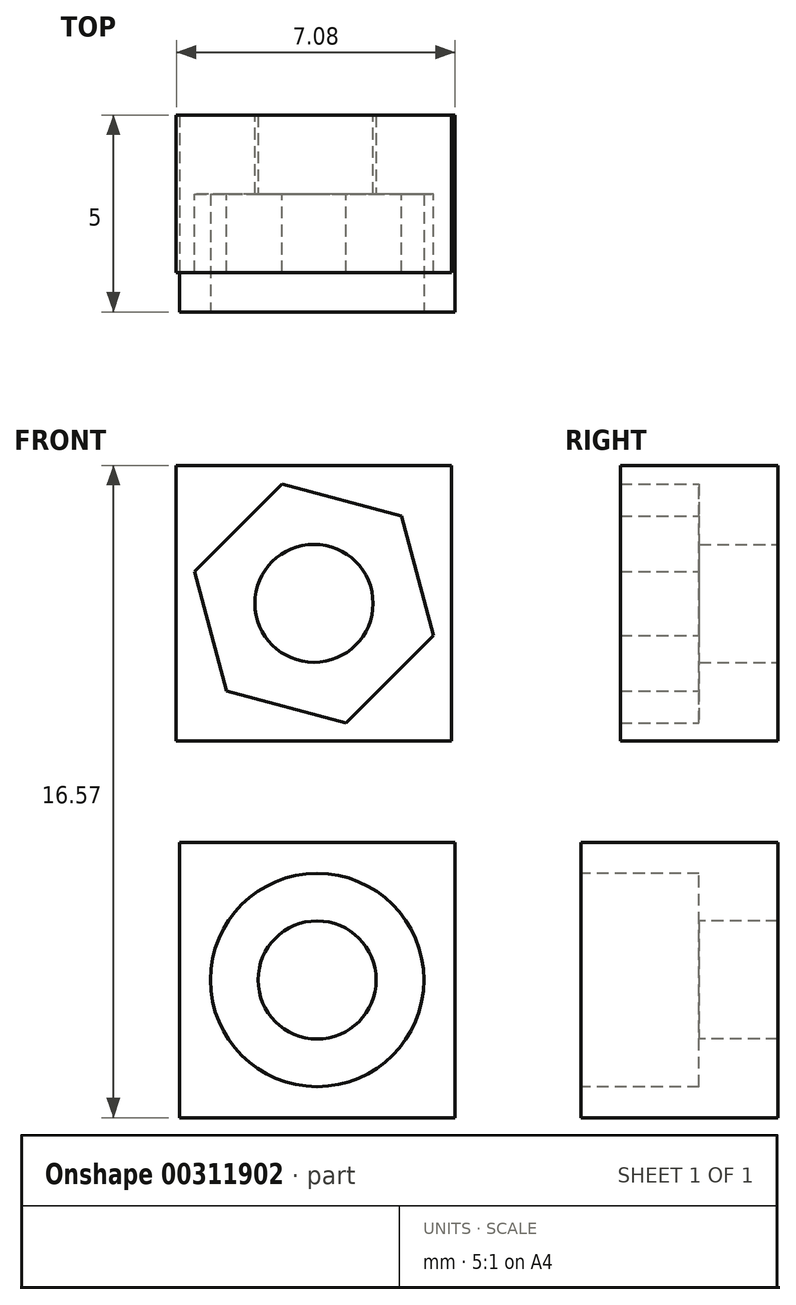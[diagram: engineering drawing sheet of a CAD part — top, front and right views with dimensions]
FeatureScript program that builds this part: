
annotation { "Feature Type Name" : "Feature", "Feature Type Description" : "" }
export const myFeature = defineFeature(function(context is Context, id is Id, definition is map)
    precondition{}
    {
        {
            var Q0;
            Q0=qCreatedBy(makeId("Front.planeOp"),FACE);
            var sketch = newSketch(context, id + "F0", { "sketchPlane" : qUnion([Q0])});
            skLineSegment(sketch, "E0.bottom", {"start": v(-25.27, 11.32) * mm, "end": v(-18.27, 11.32) * mm});
            skLineSegment(sketch, "E0.top", {"start": v(-25.27, 4.32) * mm, "end": v(-18.27, 4.32) * mm});
            skLineSegment(sketch, "E0.left", {"start": v(-25.27, 11.32) * mm, "end": v(-25.27, 4.32) * mm});
            skLineSegment(sketch, "E0.right", {"start": v(-18.27, 11.32) * mm, "end": v(-18.27, 4.32) * mm});
            skLineSegment(sketch, "E1", {"start": v(-25.27, 11.32) * mm, "end": v(-18.27, 4.32) * mm});
            skLineSegment(sketch, "E2", {"start": v(-18.27, 11.32) * mm, "end": v(-25.27, 4.32) * mm});
            skCircle(sketch, "E3", {"center": v(-21.77, 7.82) * mm, "radius": 2.7 * mm});
            skSolve(sketch);
        }
        {
            var Q0;
            {var subQ0=sQuery(id+"F0.wireOp",EDGE,"E0.bottom");Q0=makeQuery(id+"F0.imprint","IMPRINT",FACE,{"disambiguationData":[TD([[makeQuery(id+"F0.imprint","IMPRINT",EDGE,{"derivedFrom":subQ0}),-1.0]])]});}
            var Q1;
            {var subQ0=sQuery(id+"F0.wireOp",EDGE,"E0.left");Q1=makeQuery(id+"F0.imprint","IMPRINT",FACE,{"disambiguationData":[TD([[makeQuery(id+"F0.imprint","IMPRINT",EDGE,{"derivedFrom":subQ0}),1.0]])]});}
            var Q2;
            {var subQ0=sQuery(id+"F0.wireOp",EDGE,"E0.top");Q2=makeQuery(id+"F0.imprint","IMPRINT",FACE,{"disambiguationData":[TD([[makeQuery(id+"F0.imprint","IMPRINT",EDGE,{"derivedFrom":subQ0}),1.0]])]});}
            var Q3;
            {var subQ0=sQuery(id+"F0.wireOp",EDGE,"E0.right");Q3=makeQuery(id+"F0.imprint","IMPRINT",FACE,{"disambiguationData":[TD([[makeQuery(id+"F0.imprint","IMPRINT",EDGE,{"derivedFrom":subQ0}),-1.0]])]});}
            extrude(context, id + "F1", {"entities" : qUnion([Q0, Q1, Q2, Q3]), "oppositeDirection" : true, "depth" : 3 * mm});
        }
        {
            var Q0;
            Q0=makeQuery(id+"F1.opExtrude","CAP_FACE",FACE,{"disambiguationData":[OSD([sQuery(id+"F0.wireOp",EDGE,"E0.bottom"),sQuery(id+"F0.wireOp",EDGE,"E0.top"),sQuery(id+"F0.wireOp",EDGE,"E0.left"),sQuery(id+"F0.wireOp",EDGE,"E0.right"),sQuery(id+"F0.wireOp",EDGE,"E3")])],"isStart":false});
            var sketch = newSketch(context, id + "F2", { "sketchPlane" : qUnion([Q0])});
            skLineSegment(sketch, "E4", {"start": v(18.27, 11.32) * mm, "end": v(25.27, 4.32) * mm});
            skLineSegment(sketch, "E5", {"start": v(25.27, 4.32) * mm, "end": v(25.27, 11.32) * mm});
            skLineSegment(sketch, "E6", {"start": v(25.27, 11.32) * mm, "end": v(18.27, 4.32) * mm});
            skCircle(sketch, "E7", {"center": v(21.77, 7.82) * mm, "radius": 1.5 * mm});
            skSolve(sketch);
        }
        {
            var Q0;
            {var subQ1=makeQuery(id+"F1.opExtrude","CAP_EDGE",EDGE,{"disambiguationData":[OSD([sQuery(id+"F0.wireOp",EDGE,"E0.right")])],"isStart":false});Q0=makeQuery(id+"F2.imprint","IMPRINT",FACE,{"disambiguationData":[TD([[makeQuery(id+"F2.imprint","IMPRINT",EDGE,{"derivedFrom":subQ1}),1.0]])]});}
            var Q1;
            {var subQ0=sQuery(id+"F2.wireOp",EDGE,"E7");var subQ1=sQuery(id+"F2.wireOp",EDGE,"E4");var subQ2=makeQuery(id+"F2.imprint","INTERSECT",VERTEX,{"disambiguationData":[OD(0.0)],"derivedFrom":[subQ1,subQ0]});Q1=makeQuery(id+"F2.imprint","IMPRINT",FACE,{"disambiguationData":[TD([[makeQuery(id+"F2.imprint","IMPRINT",EDGE,{"disambiguationData":[TD([[subQ2,1.0]])],"derivedFrom":subQ1}),-1.0]])]});}
            var Q2;
            {var subQ0=sQuery(id+"F2.wireOp",EDGE,"E7");var subQ1=sQuery(id+"F2.wireOp",EDGE,"E4");var subQ2=makeQuery(id+"F2.imprint","INTERSECT",VERTEX,{"disambiguationData":[OD(1.0)],"derivedFrom":[subQ1,subQ0]});Q2=makeQuery(id+"F2.imprint","IMPRINT",FACE,{"disambiguationData":[TD([[makeQuery(id+"F2.imprint","IMPRINT",EDGE,{"disambiguationData":[TD([[subQ2,-1.0]])],"derivedFrom":subQ1}),-1.0]])]});}
            var Q3;
            {var subQ1=makeQuery(id+"F1.opExtrude","CAP_EDGE",EDGE,{"disambiguationData":[OSD([sQuery(id+"F0.wireOp",EDGE,"E0.top")])],"isStart":false});Q3=makeQuery(id+"F2.imprint","IMPRINT",FACE,{"disambiguationData":[TD([[makeQuery(id+"F2.imprint","IMPRINT",EDGE,{"derivedFrom":subQ1}),-1.0]])]});}
            var Q4;
            {var subQ0=sQuery(id+"F2.wireOp",EDGE,"E5");Q4=makeQuery(id+"F2.imprint","IMPRINT",FACE,{"disambiguationData":[TD([[makeQuery(id+"F2.imprint","IMPRINT",EDGE,{"derivedFrom":subQ0}),-1.0]])]});}
            var Q5;
            {var subQ0=sQuery(id+"F2.wireOp",EDGE,"E7");var subQ1=sQuery(id+"F2.wireOp",EDGE,"E4");var subQ2=makeQuery(id+"F2.imprint","INTERSECT",VERTEX,{"disambiguationData":[OD(1.0)],"derivedFrom":[subQ1,subQ0]});Q5=makeQuery(id+"F2.imprint","IMPRINT",FACE,{"disambiguationData":[TD([[makeQuery(id+"F2.imprint","IMPRINT",EDGE,{"disambiguationData":[TD([[subQ2,-1.0]])],"derivedFrom":subQ1}),1.0]])]});}
            var Q6;
            {var subQ0=sQuery(id+"F2.wireOp",EDGE,"E7");var subQ1=sQuery(id+"F2.wireOp",EDGE,"E4");var subQ2=makeQuery(id+"F2.imprint","INTERSECT",VERTEX,{"disambiguationData":[OD(0.0)],"derivedFrom":[subQ1,subQ0]});Q6=makeQuery(id+"F2.imprint","IMPRINT",FACE,{"disambiguationData":[TD([[makeQuery(id+"F2.imprint","IMPRINT",EDGE,{"disambiguationData":[TD([[subQ2,1.0]])],"derivedFrom":subQ1}),1.0]])]});}
            var Q7;
            {var subQ1=makeQuery(id+"F1.opExtrude","CAP_EDGE",EDGE,{"disambiguationData":[OSD([sQuery(id+"F0.wireOp",EDGE,"E0.bottom")])],"isStart":false});Q7=makeQuery(id+"F2.imprint","IMPRINT",FACE,{"disambiguationData":[TD([[makeQuery(id+"F2.imprint","IMPRINT",EDGE,{"derivedFrom":subQ1}),1.0]])]});}
            extrude(context, id + "F3", {"entities" : qUnion([Q0, Q1, Q2, Q3, Q4, Q5, Q6, Q7]), "operationType" : NewBodyOperationType.ADD, "depth" : 2 * mm});
        }
        {
            var Q0;
            Q0=makeQuery(id+"F3.opExtrude","CAP_FACE",FACE,{"disambiguationData":[OSD([sQuery(id+"F0.wireOp",EDGE,"E0.bottom"),sQuery(id+"F0.wireOp",EDGE,"E0.top"),sQuery(id+"F0.wireOp",EDGE,"E0.right"),sQuery(id+"F2.wireOp",EDGE,"E5"),sQuery(id+"F2.wireOp",EDGE,"E7")])],"isStart":false});
            var sketch = newSketch(context, id + "F4", { "sketchPlane" : qUnion([Q0])});
            skLineSegment(sketch, "E8.bottom", {"start": v(25.35, 13.89) * mm, "end": v(18.35, 13.89) * mm});
            skLineSegment(sketch, "E8.top", {"start": v(25.35, 20.89) * mm, "end": v(18.35, 20.89) * mm});
            skLineSegment(sketch, "E8.left", {"start": v(25.35, 13.89) * mm, "end": v(25.35, 20.89) * mm});
            skLineSegment(sketch, "E8.right", {"start": v(18.35, 13.89) * mm, "end": v(18.35, 20.89) * mm});
            skLineSegment(sketch, "E9", {"start": v(18.35, 20.89) * mm, "end": v(25.35, 13.89) * mm});
            skLineSegment(sketch, "E10", {"start": v(25.35, 20.89) * mm, "end": v(18.35, 13.89) * mm});
            skCircle(sketch, "E11", {"center": v(21.85, 17.39) * mm, "radius": 1.5 * mm});
            skSolve(sketch);
        }
        {
            var Q0;
            {var subQ0=sQuery(id+"F4.wireOp",EDGE,"E8.right");Q0=makeQuery(id+"F4.imprint","IMPRINT",FACE,{"disambiguationData":[TD([[makeQuery(id+"F4.imprint","IMPRINT",EDGE,{"derivedFrom":subQ0}),-1.0]])]});}
            var Q1;
            {var subQ0=sQuery(id+"F4.wireOp",EDGE,"E8.bottom");Q1=makeQuery(id+"F4.imprint","IMPRINT",FACE,{"disambiguationData":[TD([[makeQuery(id+"F4.imprint","IMPRINT",EDGE,{"derivedFrom":subQ0}),-1.0]])]});}
            var Q2;
            {var subQ0=sQuery(id+"F4.wireOp",EDGE,"E8.left");Q2=makeQuery(id+"F4.imprint","IMPRINT",FACE,{"disambiguationData":[TD([[makeQuery(id+"F4.imprint","IMPRINT",EDGE,{"derivedFrom":subQ0}),1.0]])]});}
            var Q3;
            {var subQ0=sQuery(id+"F4.wireOp",EDGE,"E8.top");Q3=makeQuery(id+"F4.imprint","IMPRINT",FACE,{"disambiguationData":[TD([[makeQuery(id+"F4.imprint","IMPRINT",EDGE,{"derivedFrom":subQ0}),1.0]])]});}
            extrude(context, id + "F5", {"entities" : qUnion([Q0, Q1, Q2, Q3]), "oppositeDirection" : true, "depth" : 2 * mm});
        }
        {
            var Q0;
            Q0=makeQuery(id+"F5.opExtrude","CAP_FACE",FACE,{"disambiguationData":[OSD([sQuery(id+"F4.wireOp",EDGE,"E8.bottom"),sQuery(id+"F4.wireOp",EDGE,"E8.top"),sQuery(id+"F4.wireOp",EDGE,"E8.left"),sQuery(id+"F4.wireOp",EDGE,"E8.right"),sQuery(id+"F4.wireOp",EDGE,"E11")])],"isStart":false});
            var sketch = newSketch(context, id + "F6", { "sketchPlane" : qUnion([Q0])});
            skLineSegment(sketch, "E12", {"start": v(-25.35, 20.89) * mm, "end": v(-18.35, 13.89) * mm});
            skLineSegment(sketch, "E13", {"start": v(-18.35, 20.89) * mm, "end": v(-25.35, 13.89) * mm});
            skCircle(sketch, "E14.cCircle", {"center": v(-21.85, 17.39) * mm, "radius": 1.5 * mm, "construction": true});
            skPoint(sketch, "E14.0.midPoint", {"position": v(-20.4, 17.79) * mm});
            skCircle(sketch, "E15.cCircle", {"center": v(-21.85, 17.39) * mm, "radius": 2.72 * mm, "construction": true});
            skLineSegment(sketch, "E15.0", {"start": v(-18.82, 16.57) * mm, "end": v(-21.04, 14.35) * mm});
            skLineSegment(sketch, "E15.1", {"start": v(-21.04, 14.35) * mm, "end": v(-24.08, 15.17) * mm});
            skLineSegment(sketch, "E15.2", {"start": v(-24.08, 15.17) * mm, "end": v(-24.89, 18.2) * mm});
            skLineSegment(sketch, "E15.3", {"start": v(-24.89, 18.2) * mm, "end": v(-22.67, 20.42) * mm});
            skLineSegment(sketch, "E15.4", {"start": v(-22.67, 20.42) * mm, "end": v(-19.63, 19.6) * mm});
            skLineSegment(sketch, "E15.5", {"start": v(-19.63, 19.6) * mm, "end": v(-18.82, 16.57) * mm});
            skPoint(sketch, "E15.0.midPoint", {"position": v(-19.93, 15.46) * mm});
            skSolve(sketch);
        }
        {
            var Q0;
            {var subQ1=sQuery(id+"F6.wireOp",EDGE,"E15.2");Q0=makeQuery(id+"F6.imprint","IMPRINT",FACE,{"disambiguationData":[TD([[makeQuery(id+"F6.imprint","IMPRINT",EDGE,{"derivedFrom":subQ1}),1.0]])]});}
            var Q1;
            {var subQ0=sQuery(id+"F6.wireOp",EDGE,"E15.1");Q1=makeQuery(id+"F6.imprint","IMPRINT",FACE,{"disambiguationData":[TD([[makeQuery(id+"F6.imprint","IMPRINT",EDGE,{"derivedFrom":subQ0}),1.0]])]});}
            var Q2;
            {var subQ0=sQuery(id+"F6.wireOp",EDGE,"E15.5");Q2=makeQuery(id+"F6.imprint","IMPRINT",FACE,{"disambiguationData":[TD([[makeQuery(id+"F6.imprint","IMPRINT",EDGE,{"derivedFrom":subQ0}),1.0]])]});}
            var Q3;
            {var subQ0=sQuery(id+"F6.wireOp",EDGE,"E15.4");Q3=makeQuery(id+"F6.imprint","IMPRINT",FACE,{"disambiguationData":[TD([[makeQuery(id+"F6.imprint","IMPRINT",EDGE,{"derivedFrom":subQ0}),1.0]])]});}
            extrude(context, id + "F7", {"entities" : qUnion([Q0, Q1, Q2, Q3]), "operationType" : NewBodyOperationType.ADD, "depth" : 2 * mm});
        }
    });
